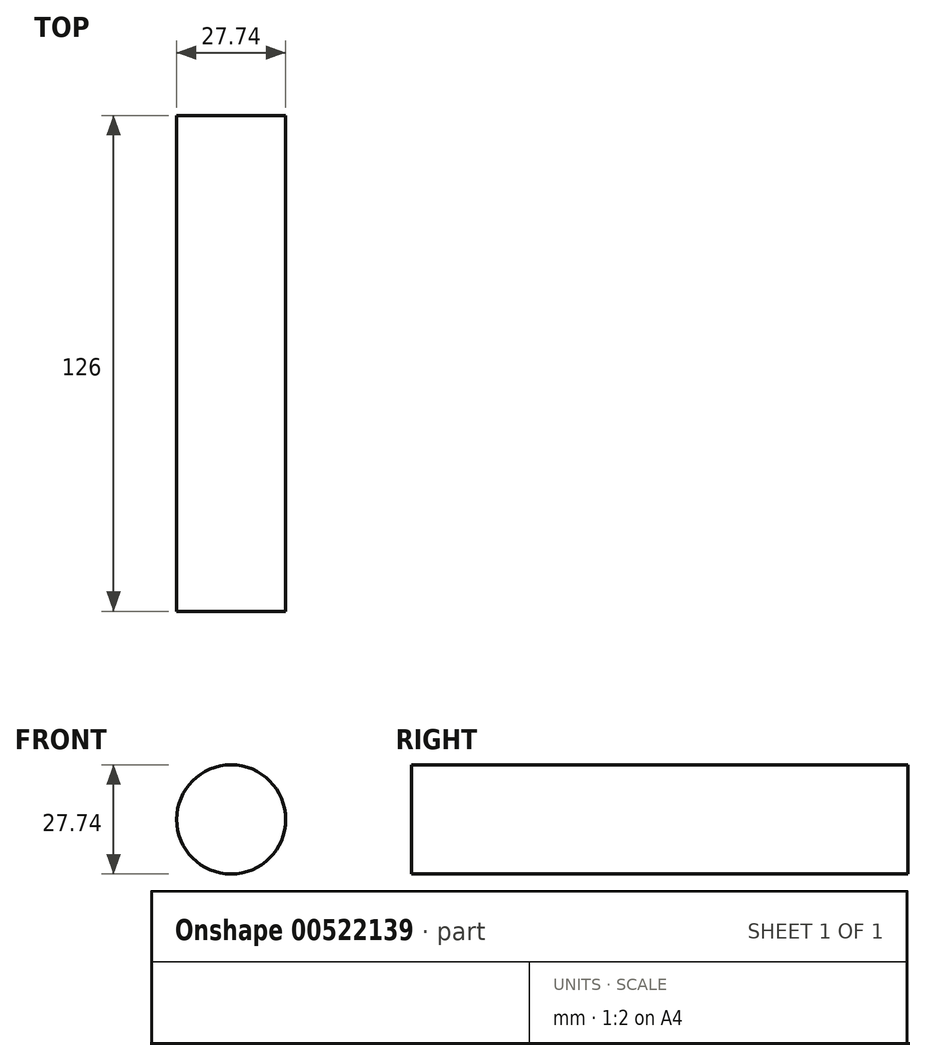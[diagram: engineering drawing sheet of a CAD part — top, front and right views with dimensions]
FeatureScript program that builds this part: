
annotation { "Feature Type Name" : "Feature", "Feature Type Description" : "" }
export const myFeature = defineFeature(function(context is Context, id is Id, definition is map)
    precondition{}
    {
        {
            var Q0;
            Q0=qCreatedBy(makeId("Front.planeOp"),FACE);
            var sketch = newSketch(context, id + "F0", { "sketchPlane" : qUnion([Q0])});
            skPoint(sketch, "E0.middle", {"position": v(0, 0) * mm});
            skCircle(sketch, "E1", {"center": v(0, -54.3) * mm, "radius": 38.95 * mm});
            skCircle(sketch, "E2", {"center": v(0, 54.3) * mm, "radius": 13.87 * mm});
            skCircle(sketch, "E3.MirrorC", {"center": v(0, -54.3) * mm, "radius": 13.87 * mm});
            skSolve(sketch);
        }
        {
            var Q0;
            Q0=makeQuery(id+"F0.imprint","IMPRINT",FACE,{"disambiguationData":[TD([[makeQuery(id+"F0.imprint","IMPRINT",EDGE,{"derivedFrom":sQuery(id+"F0.wireOp",EDGE,"E3.MirrorC")}),1.0]])]});
            var Q1;
            {var subQ1=sQuery(id+"F0.wireOp",EDGE,"E0.left");Q1=makeQuery(id+"F0.imprint","IMPRINT",FACE,{"disambiguationData":[TD([[makeQuery(id+"F0.imprint","IMPRINT",EDGE,{"derivedFrom":subQ1}),1.0]])]});}
            extrude(context, id + "F1", {"entities" : qUnion([Q0, Q1]), "endBound" : BoundingType.SYMMETRIC, "depth" : 126 * mm, "offsetDistance" : 25 * mm});
        }
    });
